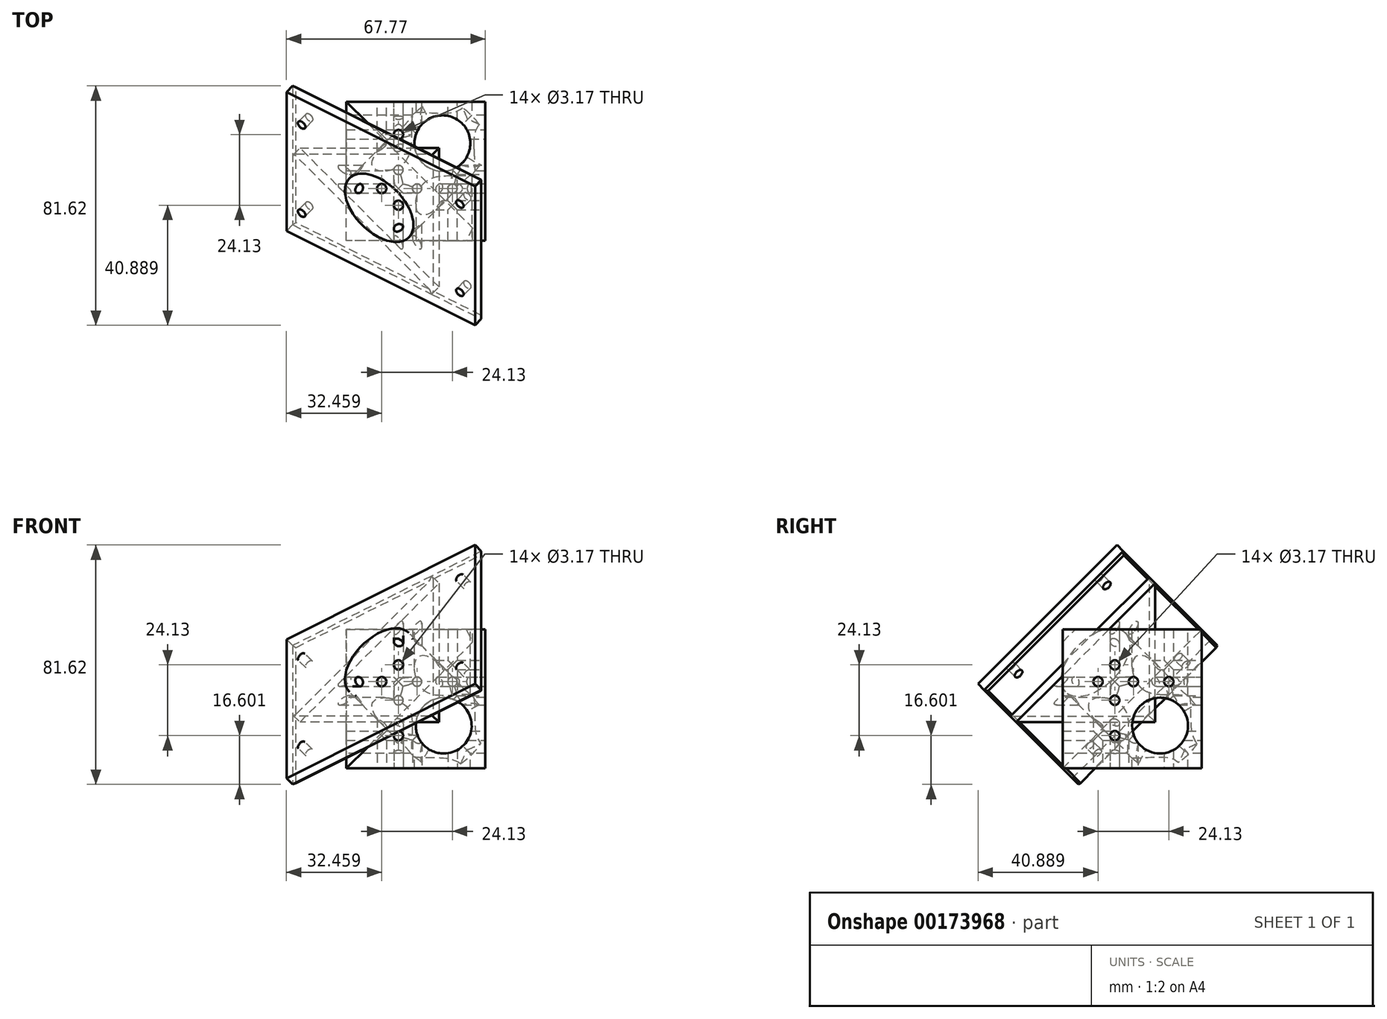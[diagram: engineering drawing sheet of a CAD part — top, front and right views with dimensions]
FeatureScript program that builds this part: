
annotation { "Feature Type Name" : "Feature", "Feature Type Description" : "" }
export const myFeature = defineFeature(function(context is Context, id is Id, definition is map)
    precondition{}
    {
        {
            var Q0;
            Q0=qCreatedBy(makeId("Top.planeOp"),FACE);
            var sketch = newSketch(context, id + "F0", { "sketchPlane" : qUnion([Q0])});
            skLineSegment(sketch, "E0", {"start": v(0, 0) * mm, "end": v(23.69, 0) * mm});
            skLineSegment(sketch, "E1", {"start": v(23.69, 0) * mm, "end": v(23.69, 23.69) * mm});
            skLineSegment(sketch, "E2", {"start": v(23.69, 23.69) * mm, "end": v(0, 23.69) * mm});
            skLineSegment(sketch, "E3", {"start": v(0, 23.69) * mm, "end": v(0, 0) * mm});
            skLineSegment(sketch, "E4.MirrorCS", {"start": v(23.69, 0) * mm, "end": v(23.69, -23.69) * mm});
            skLineSegment(sketch, "E5.MirrorCS", {"start": v(23.69, -23.69) * mm, "end": v(0, -23.69) * mm});
            skLineSegment(sketch, "E6.MirrorCS", {"start": v(0, -23.69) * mm, "end": v(0, 0) * mm});
            skLineSegment(sketch, "E7.MirrorCS", {"start": v(-23.69, 23.69) * mm, "end": v(0, 23.69) * mm});
            skLineSegment(sketch, "E8.MirrorCS", {"start": v(-23.69, 0) * mm, "end": v(-23.69, 23.69) * mm});
            skLineSegment(sketch, "E9.MirrorCS", {"start": v(-23.69, 0) * mm, "end": v(-23.69, -23.69) * mm});
            skLineSegment(sketch, "E10.MirrorCS", {"start": v(-23.69, -23.69) * mm, "end": v(0, -23.69) * mm});
            skSolve(sketch);
        }
        {
            var Q0;
            Q0=qSketchRegion(id+"F0",true);
            extrude(context, id + "F1", {"entities" : qUnion([Q0]), "depth" : 23.7 * mm});
        }
        {
            var Q0;
            Q0=qSketchRegion(id+"F0",true);
            extrude(context, id + "F2", {"entities" : qUnion([Q0]), "operationType" : NewBodyOperationType.ADD, "oppositeDirection" : true, "depth" : 23.7 * mm});
        }
        {
            var Q0;
            Q0=makeQuery(id+"F1.opExtrude","CAP_VERTEX",VERTEX,{"disambiguationData":[OSD([sQuery(id+"F0.wireOp",EDGE,"E7.MirrorCS"),sQuery(id+"F0.wireOp",EDGE,"E8.MirrorCS")])],"isStart":false});
            var Q1;
            Q1=makeQuery(id+"F1.opExtrude","CAP_VERTEX",VERTEX,{"disambiguationData":[OSD([sQuery(id+"F0.wireOp",EDGE,"E4.MirrorCS"),sQuery(id+"F0.wireOp",EDGE,"E5.MirrorCS")])],"isStart":false});
            var Q2;
            Q2=makeQuery(id+"F2.opExtrude","CAP_VERTEX",VERTEX,{"disambiguationData":[OSD([sQuery(id+"F0.wireOp",EDGE,"E9.MirrorCS"),sQuery(id+"F0.wireOp",EDGE,"E10.MirrorCS")])],"isStart":false});
            cPlane(context, id + "F3", {"entities" : qUnion([Q0, Q1, Q2]), "cplaneType" : CPlaneType.THREE_POINT, "offset" : 25.4 * mm, "width" : 152.4 * mm, "height" : 152.4 * mm});
        }
        {
            var Q0;
            Q0=qCreatedBy(id+"F3.planeOp",FACE);
            var sketch = newSketch(context, id + "F4", { "sketchPlane" : qUnion([Q0])});
            skLineSegment(sketch, "E11", {"start": v(33.43, -38.75) * mm, "end": v(33.43, 45.77) * mm});
            skLineSegment(sketch, "E12", {"start": v(33.43, 45.77) * mm, "end": v(-49.12, 45.77) * mm});
            skLineSegment(sketch, "E13", {"start": v(-49.12, 45.77) * mm, "end": v(-49.12, -38.75) * mm});
            skLineSegment(sketch, "E14", {"start": v(-49.12, -38.75) * mm, "end": v(33.43, -38.75) * mm});
            skSolve(sketch);
        }
        {
            var Q0;
            Q0=qSketchRegion(id+"F4",true);
            extrude(context, id + "F5", {"entities" : qUnion([Q0]), "operationType" : NewBodyOperationType.REMOVE, "depth" : 50.8 * mm});
        }
        {
            var Q0;
            Q0=makeQuery(id+"F5.boolean.opBoolean","COPY",FACE,{"derivedFrom":makeQuery(id+"F5.opExtrude","CAP_FACE",FACE,{"disambiguationData":[OSD([sQuery(id+"F4.wireOp",EDGE,"E11"),sQuery(id+"F4.wireOp",EDGE,"E12"),sQuery(id+"F4.wireOp",EDGE,"E13"),sQuery(id+"F4.wireOp",EDGE,"E14")])],"isStart":true})});
            var sketch = newSketch(context, id + "F6", { "sketchPlane" : qUnion([Q0])});
            skLineSegment(sketch, "E15", {"start": v(19.34, 33.5) * mm, "end": v(19.34, -33.5) * mm});
            skLineSegment(sketch, "E16", {"start": v(19.34, -33.5) * mm, "end": v(-38.68, 0) * mm});
            skLineSegment(sketch, "E17", {"start": v(-38.68, 0) * mm, "end": v(19.34, 33.5) * mm});
            skSolve(sketch);
        }
        {
            var Q0;
            Q0=qSketchRegion(id+"F6",true);
            extrude(context, id + "F7", {"entities" : qUnion([Q0]), "operationType" : NewBodyOperationType.ADD, "depth" : 7.94 * mm});
        }
        {
            var Q0;
            Q0=makeQuery(id+"F7.opExtrude","CAP_FACE",FACE,{"disambiguationData":[OSD([sQuery(id+"F6.wireOp",EDGE,"E15"),sQuery(id+"F6.wireOp",EDGE,"E16"),sQuery(id+"F6.wireOp",EDGE,"E17")])],"isStart":false});
            var sketch = newSketch(context, id + "F8", { "sketchPlane" : qUnion([Q0])});
            skLineSegment(sketch, "E18", {"start": v(19.34, 33.5) * mm, "end": v(-9.67, -16.75) * mm});
            skLineSegment(sketch, "E19", {"start": v(19.34, -33.5) * mm, "end": v(-9.67, 16.75) * mm});
            skLineSegment(sketch, "E20", {"start": v(-38.68, 0) * mm, "end": v(19.34, 0) * mm});
            skCircle(sketch, "E21", {"center": v(0, 0) * mm, "radius": 14.29 * mm});
            skSolve(sketch);
        }
        {
            var Q0;
            Q0=qSketchRegion(id+"F8",true);
            extrude(context, id + "F9", {"entities" : qUnion([Q0]), "operationType" : NewBodyOperationType.REMOVE, "oppositeDirection" : true, "depth" : 44.45 * mm});
        }
        {
            var Q0;
            Q0=makeQuery(id+"F1.opExtrude","CAP_FACE",FACE,{"disambiguationData":[OSD([sQuery(id+"F0.wireOp",EDGE,"E1"),sQuery(id+"F0.wireOp",EDGE,"E2"),sQuery(id+"F0.wireOp",EDGE,"E4.MirrorCS"),sQuery(id+"F0.wireOp",EDGE,"E5.MirrorCS"),sQuery(id+"F0.wireOp",EDGE,"E7.MirrorCS"),sQuery(id+"F0.wireOp",EDGE,"E8.MirrorCS"),sQuery(id+"F0.wireOp",EDGE,"E9.MirrorCS"),sQuery(id+"F0.wireOp",EDGE,"E10.MirrorCS")])],"isStart":false});
            var sketch = newSketch(context, id + "F10", { "sketchPlane" : qUnion([Q0])});
            skCircle(sketch, "E22", {"center": v(9.08, 9.53) * mm, "radius": 9.53 * mm});
            skSolve(sketch);
        }
        {
            var Q0;
            Q0=qSketchRegion(id+"F10",true);
            extrude(context, id + "F11", {"entities" : qUnion([Q0]), "operationType" : NewBodyOperationType.REMOVE, "oppositeDirection" : true, "depth" : 76.2 * mm});
        }
        {
            var Q0;
            {var subQ0=sQuery(id+"F0.wireOp",EDGE,"E9.MirrorCS");var subQ1=sQuery(id+"F0.wireOp",EDGE,"E8.MirrorCS");Q0=makeQuery(id+"F2.boolean.opBoolean","MERGE",FACE,{"derivedFrom":[makeQuery(id+"F1.opExtrude","SWEPT_FACE",FACE,{"disambiguationData":[OSD([subQ1,subQ0])]}),makeQuery(id+"F2.opExtrude","SWEPT_FACE",FACE,{"disambiguationData":[OSD([subQ1,subQ0])]})]});}
            var sketch = newSketch(context, id + "F12", { "sketchPlane" : qUnion([Q0])});
            skCircle(sketch, "E23", {"center": v(-9.53, -9.08) * mm, "radius": 9.53 * mm});
            skSolve(sketch);
        }
        {
            var Q0;
            Q0=qSketchRegion(id+"F12",true);
            extrude(context, id + "F13", {"entities" : qUnion([Q0]), "operationType" : NewBodyOperationType.REMOVE, "oppositeDirection" : true, "depth" : 76.2 * mm});
        }
        {
            var Q0;
            {var subQ0=sQuery(id+"F0.wireOp",EDGE,"E10.MirrorCS");var subQ1=sQuery(id+"F0.wireOp",EDGE,"E5.MirrorCS");Q0=makeQuery(id+"F2.boolean.opBoolean","MERGE",FACE,{"derivedFrom":[makeQuery(id+"F1.opExtrude","SWEPT_FACE",FACE,{"disambiguationData":[OSD([subQ1,subQ0])]}),makeQuery(id+"F2.opExtrude","SWEPT_FACE",FACE,{"disambiguationData":[OSD([subQ1,subQ0])]})]});}
            var sketch = newSketch(context, id + "F14", { "sketchPlane" : qUnion([Q0])});
            skCircle(sketch, "E24", {"center": v(9.53, -9.08) * mm, "radius": 9.53 * mm});
            skSolve(sketch);
        }
        {
            var Q0;
            Q0=qSketchRegion(id+"F14",true);
            extrude(context, id + "F15", {"entities" : qUnion([Q0]), "operationType" : NewBodyOperationType.REMOVE, "oppositeDirection" : true, "depth" : 76.2 * mm});
        }
        {
            var Q0;
            {var subQ0=sQuery(id+"F0.wireOp",EDGE,"E4.MirrorCS");var subQ1=sQuery(id+"F0.wireOp",EDGE,"E1");Q0=makeQuery(id+"F2.boolean.opBoolean","MERGE",FACE,{"derivedFrom":[makeQuery(id+"F1.opExtrude","SWEPT_FACE",FACE,{"disambiguationData":[OSD([subQ1,subQ0])]}),makeQuery(id+"F2.opExtrude","SWEPT_FACE",FACE,{"disambiguationData":[OSD([subQ1,subQ0])]})]});}
            var sketch = newSketch(context, id + "F16", { "sketchPlane" : qUnion([Q0])});
            skCircle(sketch, "E25", {"center": v(-11.62, 5.9) * mm, "radius": 1.59 * mm});
            skCircle(sketch, "E26", {"center": v(12.5, 5.9) * mm, "radius": 1.59 * mm});
            skCircle(sketch, "E27", {"center": v(-5.9, -12.5) * mm, "radius": 1.59 * mm});
            skCircle(sketch, "E28", {"center": v(-5.9, 11.62) * mm, "radius": 1.59 * mm});
            skCircle(sketch, "E29", {"center": v(0.44, 5.9) * mm, "radius": 1.59 * mm});
            skCircle(sketch, "E30", {"center": v(-5.9, -0.44) * mm, "radius": 1.59 * mm});
            skSolve(sketch);
        }
        {
            var Q0;
            Q0=qSketchRegion(id+"F16",true);
            extrude(context, id + "F17", {"entities" : qUnion([Q0]), "operationType" : NewBodyOperationType.REMOVE, "oppositeDirection" : true, "depth" : 50.8 * mm});
        }
        {
            var Q0;
            Q0=makeQuery(id+"F2.opExtrude","CAP_FACE",FACE,{"disambiguationData":[OSD([sQuery(id+"F0.wireOp",EDGE,"E1"),sQuery(id+"F0.wireOp",EDGE,"E2"),sQuery(id+"F0.wireOp",EDGE,"E4.MirrorCS"),sQuery(id+"F0.wireOp",EDGE,"E5.MirrorCS"),sQuery(id+"F0.wireOp",EDGE,"E7.MirrorCS"),sQuery(id+"F0.wireOp",EDGE,"E8.MirrorCS"),sQuery(id+"F0.wireOp",EDGE,"E9.MirrorCS"),sQuery(id+"F0.wireOp",EDGE,"E10.MirrorCS")])],"isStart":false});
            var sketch = newSketch(context, id + "F18", { "sketchPlane" : qUnion([Q0])});
            skCircle(sketch, "E31", {"center": v(-5.9, 11.62) * mm, "radius": 1.59 * mm});
            skCircle(sketch, "E32", {"center": v(-5.9, -0.44) * mm, "radius": 1.59 * mm});
            skCircle(sketch, "E33", {"center": v(-5.9, -12.5) * mm, "radius": 1.59 * mm});
            skCircle(sketch, "E34", {"center": v(12.5, 5.9) * mm, "radius": 1.59 * mm});
            skCircle(sketch, "E35", {"center": v(0.44, 5.9) * mm, "radius": 1.59 * mm});
            skCircle(sketch, "E36", {"center": v(-11.62, 5.9) * mm, "radius": 1.59 * mm});
            skSolve(sketch);
        }
        {
            var Q0;
            Q0=qSketchRegion(id+"F18",true);
            extrude(context, id + "F19", {"entities" : qUnion([Q0]), "operationType" : NewBodyOperationType.REMOVE, "oppositeDirection" : true, "depth" : 50.8 * mm});
        }
        {
            var Q0;
            {var subQ0=sQuery(id+"F0.wireOp",EDGE,"E7.MirrorCS");var subQ1=sQuery(id+"F0.wireOp",EDGE,"E2");Q0=makeQuery(id+"F2.boolean.opBoolean","MERGE",FACE,{"derivedFrom":[makeQuery(id+"F1.opExtrude","SWEPT_FACE",FACE,{"disambiguationData":[OSD([subQ1,subQ0])]}),makeQuery(id+"F2.opExtrude","SWEPT_FACE",FACE,{"disambiguationData":[OSD([subQ1,subQ0])]})]});}
            var sketch = newSketch(context, id + "F20", { "sketchPlane" : qUnion([Q0])});
            skCircle(sketch, "E37", {"center": v(-12.5, 5.9) * mm, "radius": 1.59 * mm});
            skCircle(sketch, "E38", {"center": v(-0.44, 5.9) * mm, "radius": 1.59 * mm});
            skCircle(sketch, "E39", {"center": v(11.62, 5.9) * mm, "radius": 1.59 * mm});
            skCircle(sketch, "E40", {"center": v(5.9, -0.44) * mm, "radius": 1.59 * mm});
            skCircle(sketch, "E41", {"center": v(5.9, -12.5) * mm, "radius": 1.59 * mm});
            skCircle(sketch, "E42", {"center": v(5.9, 11.62) * mm, "radius": 1.59 * mm});
            skSolve(sketch);
        }
        {
            var Q0;
            Q0=qSketchRegion(id+"F20",true);
            extrude(context, id + "F21", {"entities" : qUnion([Q0]), "operationType" : NewBodyOperationType.REMOVE, "oppositeDirection" : true, "depth" : 50.8 * mm});
        }
        {
            var Q0;
            Q0=makeQuery(id+"FqqhvvFNBQSlBQT_1.boolean.opBoolean","MERGE",FACE,{"derivedFrom":[makeQuery(id+"F7.opExtrude","CAP_FACE",FACE,{"disambiguationData":[OSD([sQuery(id+"F6.wireOp",EDGE,"E15"),sQuery(id+"F6.wireOp",EDGE,"E16"),sQuery(id+"F6.wireOp",EDGE,"E17")])],"isStart":false}),makeQuery(id+"FqqhvvFNBQSlBQT_1.opExtrude","CAP_FACE",FACE,{"disambiguationData":[OSD([sQuery(id+"FxdyyoIKbvKMV77_1.wireOp",EDGE,"y0KdcDTT-Omlm-p4Xv-BQxv-HzK8azKeJ4t5")])],"isStart":true})]});
            var sketch = newSketch(context, id + "F22", { "sketchPlane" : qUnion([Q0])});
            skLineSegment(sketch, "E43", {"start": v(19.34, -33.5) * mm, "end": v(40.04, -33.5) * mm});
            skLineSegment(sketch, "E44", {"start": v(40.04, -33.5) * mm, "end": v(40.04, 33.5) * mm});
            skLineSegment(sketch, "E45", {"start": v(40.04, 33.5) * mm, "end": v(19.34, 33.5) * mm});
            skLineSegment(sketch, "E46", {"start": v(19.34, 33.5) * mm, "end": v(19.34, -33.5) * mm});
            skLineSegment(sketch, "E47", {"start": v(19.34, -33.5) * mm, "end": v(-38.7, -33.5) * mm});
            skLineSegment(sketch, "E48", {"start": v(-38.7, 33.5) * mm, "end": v(-38.7, -33.5) * mm});
            skLineSegment(sketch, "E49", {"start": v(-38.7, 33.5) * mm, "end": v(19.34, 33.5) * mm});
            skSolve(sketch);
        }
        {
            var Q0;
            Q0=qSketchRegion(id+"F22",true);
            extrude(context, id + "F23", {"entities" : qUnion([Q0]), "operationType" : NewBodyOperationType.ADD, "oppositeDirection" : true, "depth" : 4.44 * mm});
        }
        {
            var Q0;
            Q0=makeQuery(id+"F23.boolean.opBoolean","MERGE",FACE,{"derivedFrom":[makeQuery(id+"FqqhvvFNBQSlBQT_1.boolean.opBoolean","MERGE",FACE,{"derivedFrom":[makeQuery(id+"F7.opExtrude","CAP_FACE",FACE,{"disambiguationData":[OSD([sQuery(id+"F6.wireOp",EDGE,"E15"),sQuery(id+"F6.wireOp",EDGE,"E16"),sQuery(id+"F6.wireOp",EDGE,"E17")])],"isStart":false}),makeQuery(id+"FqqhvvFNBQSlBQT_1.opExtrude","CAP_FACE",FACE,{"disambiguationData":[OSD([sQuery(id+"FxdyyoIKbvKMV77_1.wireOp",EDGE,"y0KdcDTT-Omlm-p4Xv-BQxv-HzK8azKeJ4t5")])],"isStart":true})]}),makeQuery(id+"F23.opExtrude","CAP_FACE",FACE,{"disambiguationData":[OSD([sQuery(id+"F22.wireOp",EDGE,"E43"),sQuery(id+"F22.wireOp",EDGE,"E44"),sQuery(id+"F22.wireOp",EDGE,"E45"),sQuery(id+"F22.wireOp",EDGE,"E47"),sQuery(id+"F22.wireOp",EDGE,"E48"),sQuery(id+"F22.wireOp",EDGE,"E49")])],"isStart":true})]});
            var sketch = newSketch(context, id + "F24", { "sketchPlane" : qUnion([Q0])});
            skCircle(sketch, "E50", {"center": v(33.7, -21.27) * mm, "radius": 1.59 * mm});
            skCircle(sketch, "E51", {"center": v(33.7, 21.28) * mm, "radius": 1.59 * mm});
            skCircle(sketch, "E52", {"center": v(-32.35, 21.28) * mm, "radius": 1.59 * mm});
            skCircle(sketch, "E53", {"center": v(-32.35, -21.27) * mm, "radius": 1.59 * mm});
            skCircle(sketch, "E54", {"center": v(0, 0) * mm, "radius": 14.29 * mm});
            skSolve(sketch);
        }
        {
            var Q0;
            Q0 = qSketchRegion(id + "F24", true);
            extrude(context, id + "F25", {"entities" : qUnion([Q0]), "operationType" : NewBodyOperationType.REMOVE, "oppositeDirection" : true, "depth" : 25.4 * mm});
        }
        {
            var Q0;
            Q0=makeQuery(id+"F23.opExtrude","CAP_EDGE",EDGE,{"disambiguationData":[OSD([sQuery(id+"F22.wireOp",EDGE,"E48")])],"isStart":false});
            var Q1;
            {var subQ0=sQuery(id+"F22.wireOp",EDGE,"E49");var subQ1=sQuery(id+"F22.wireOp",EDGE,"E45");var subQ2=sQuery(id+"F22.wireOp",EDGE,"E48");Q1=makeQuery(id+"F23.boolean.opBoolean","SPLIT",EDGE,{"disambiguationData":[TD([makeQuery(id+"F23.opExtrude","SWEPT_FACE",FACE,{"disambiguationData":[OSD([subQ2])]})])],"derivedFrom":makeQuery(id+"F23.opExtrude","CAP_EDGE",EDGE,{"disambiguationData":[OSD([subQ1,subQ0])],"isStart":false})});}
            var Q2;
            Q2=makeQuery(id+"F23.opExtrude","CAP_EDGE",EDGE,{"disambiguationData":[OSD([sQuery(id+"F22.wireOp",EDGE,"E44")])],"isStart":false});
            var Q3;
            {var subQ0=sQuery(id+"F22.wireOp",EDGE,"E47");var subQ1=sQuery(id+"F22.wireOp",EDGE,"E43");var subQ2=sQuery(id+"F22.wireOp",EDGE,"E44");Q3=makeQuery(id+"F23.boolean.opBoolean","SPLIT",EDGE,{"disambiguationData":[TD([makeQuery(id+"F23.opExtrude","SWEPT_FACE",FACE,{"disambiguationData":[OSD([subQ2])]})])],"derivedFrom":makeQuery(id+"F23.opExtrude","CAP_EDGE",EDGE,{"disambiguationData":[OSD([subQ1,subQ0])],"isStart":false})});}
            var Q4;
            {var subQ0=sQuery(id+"F22.wireOp",EDGE,"E44");var subQ1=sQuery(id+"F22.wireOp",EDGE,"E49");var subQ2=sQuery(id+"F22.wireOp",EDGE,"E45");Q4=makeQuery(id+"F23.boolean.opBoolean","SPLIT",EDGE,{"disambiguationData":[TD([makeQuery(id+"F23.opExtrude","SWEPT_FACE",FACE,{"disambiguationData":[OSD([subQ0])]})])],"derivedFrom":makeQuery(id+"F23.opExtrude","CAP_EDGE",EDGE,{"disambiguationData":[OSD([subQ2,subQ1])],"isStart":false})});}
            var Q5;
            {var subQ0=sQuery(id+"F22.wireOp",EDGE,"E47");var subQ1=sQuery(id+"F22.wireOp",EDGE,"E43");var subQ2=sQuery(id+"F22.wireOp",EDGE,"E48");Q5=makeQuery(id+"F23.boolean.opBoolean","SPLIT",EDGE,{"disambiguationData":[TD([makeQuery(id+"F23.opExtrude","SWEPT_FACE",FACE,{"disambiguationData":[OSD([subQ2])]})])],"derivedFrom":makeQuery(id+"F23.opExtrude","CAP_EDGE",EDGE,{"disambiguationData":[OSD([subQ1,subQ0])],"isStart":false})});}
            chamfer(context, id + "F26", {"entities" : qUnion([Q0, Q1, Q2, Q3, Q4, Q5]), "width" : 0.8 * mm, "tangentPropagation" : true});
        }
    });
